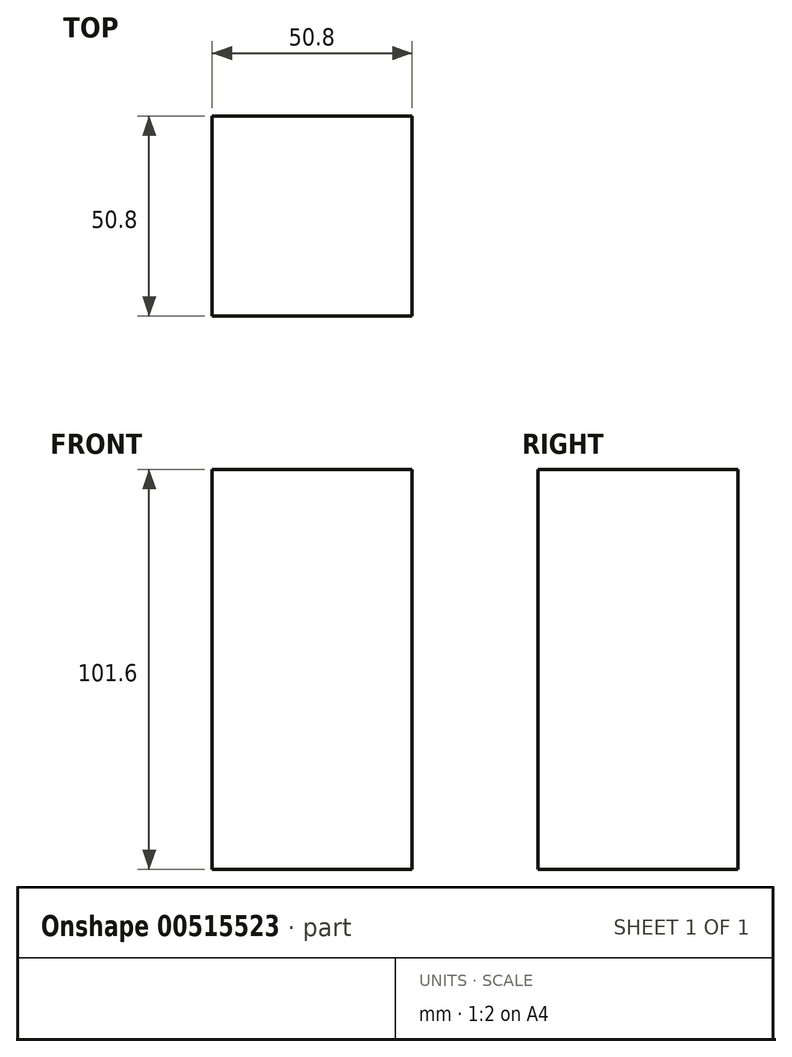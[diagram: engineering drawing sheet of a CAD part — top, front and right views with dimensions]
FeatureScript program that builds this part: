
annotation { "Feature Type Name" : "Feature", "Feature Type Description" : "" }
export const myFeature = defineFeature(function(context is Context, id is Id, definition is map)
    precondition{}
    {
        {
            var Q0;
            Q0=qCreatedBy(makeId("Right.planeOp"),FACE);
            var sketch = newSketch(context, id + "F0", { "sketchPlane" : qUnion([Q0])});
            skLineSegment(sketch, "E0.bottom", {"start": v(25.4, 50.8) * mm, "end": v(-25.4, 50.8) * mm});
            skLineSegment(sketch, "E0.top", {"start": v(25.4, -50.8) * mm, "end": v(-25.4, -50.8) * mm});
            skLineSegment(sketch, "E0.left", {"start": v(25.4, 50.8) * mm, "end": v(25.4, -50.8) * mm});
            skLineSegment(sketch, "E0.right", {"start": v(-25.4, 50.8) * mm, "end": v(-25.4, -50.8) * mm});
            skPoint(sketch, "E0.middle", {"position": v(0, 0) * mm});
            skSolve(sketch);
        }
        {
            var Q0;
            Q0=makeQuery(id+"F0.imprint","IMPRINT",FACE,{"disambiguationData":[TD([[makeQuery(id+"F0.imprint","IMPRINT",EDGE,{"derivedFrom":sQuery(id+"F0.wireOp",EDGE,"E0.bottom")}),1.0]])]});
            extrude(context, id + "F1", {"entities" : qUnion([Q0]), "oppositeDirection" : true, "depth" : 50.8 * mm, "offsetDistance" : 25.4 * mm});
        }
    });
